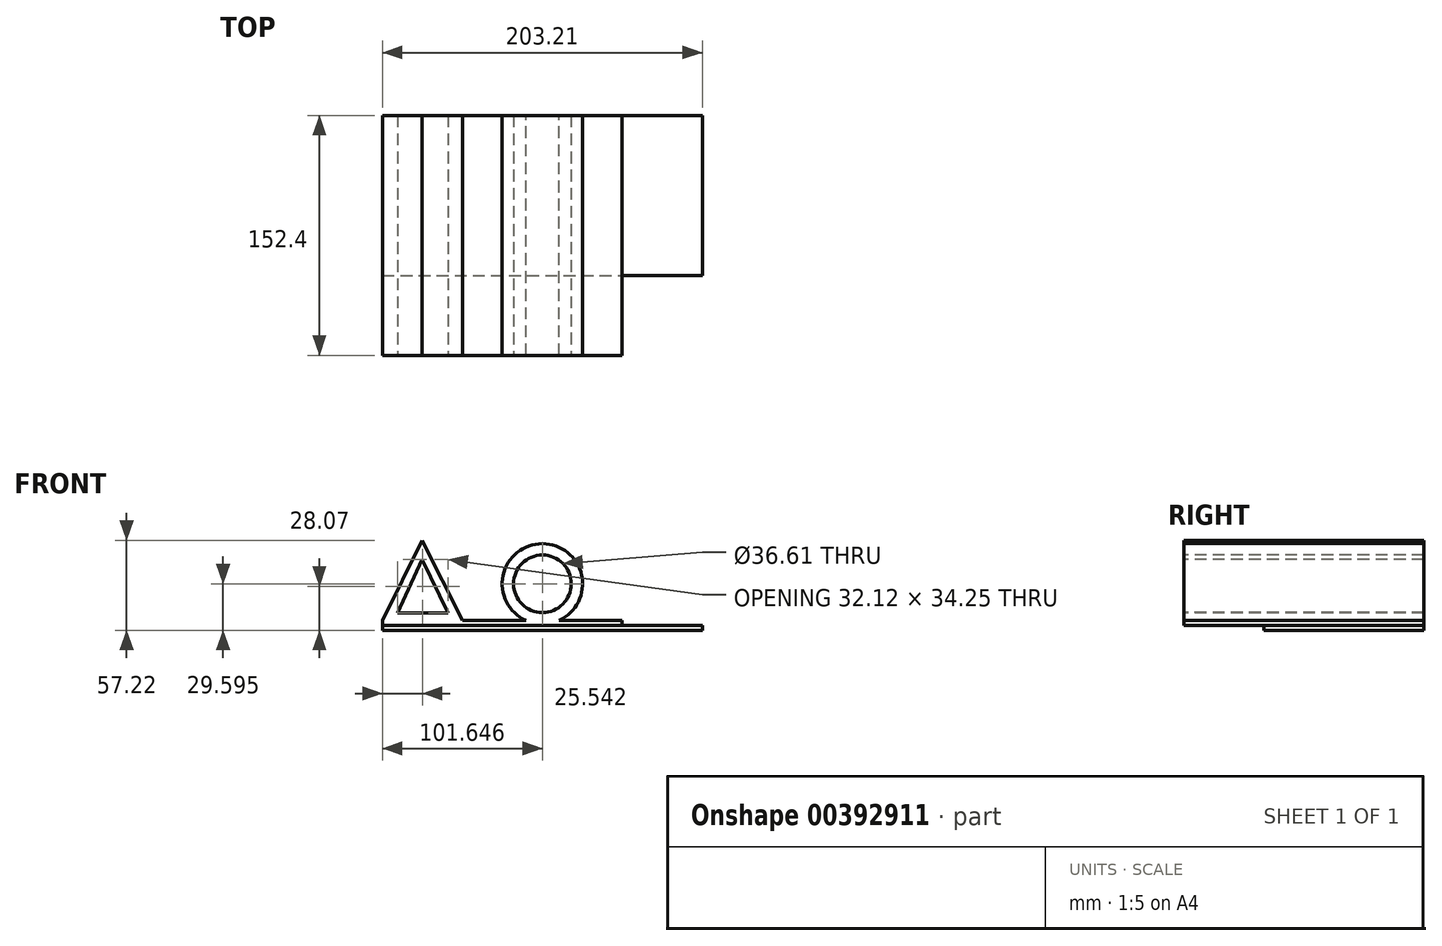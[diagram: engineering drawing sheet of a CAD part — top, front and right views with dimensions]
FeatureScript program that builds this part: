
annotation { "Feature Type Name" : "Feature", "Feature Type Description" : "" }
export const myFeature = defineFeature(function(context is Context, id is Id, definition is map)
    precondition{}
    {
        {
            var Q0;
            Q0=qCreatedBy(makeId("Top.planeOp"),FACE);
            var sketch = newSketch(context, id + "F0", { "sketchPlane" : qUnion([Q0])});
            skLineSegment(sketch, "E0.bottom", {"start": v(101.6, -152.4) * mm, "end": v(-101.6, -152.4) * mm});
            skLineSegment(sketch, "E0.top", {"start": v(101.6, 152.4) * mm, "end": v(-101.6, 152.4) * mm});
            skLineSegment(sketch, "E0.left", {"start": v(101.6, -152.4) * mm, "end": v(101.6, 152.4) * mm});
            skLineSegment(sketch, "E0.right", {"start": v(-101.6, -152.4) * mm, "end": v(-101.6, 152.4) * mm});
            skPoint(sketch, "E0.middle", {"position": v(0, 0) * mm});
            skSolve(sketch);
        }
        {
            var Q0;
            Q0=makeQuery(id+"F0.imprint","IMPRINT",FACE,{"disambiguationData":[TD([[makeQuery(id+"F0.imprint","IMPRINT",EDGE,{"derivedFrom":sQuery(id+"F0.wireOp",EDGE,"E0.bottom")}),-1.0]])]});
            extrude(context, id + "F1", {"entities" : qUnion([Q0]), "depth" : 6.35 * mm});
        }
        {
            var Q0;
            Q0=qCreatedBy(makeId("Front.planeOp"),FACE);
            var sketch = newSketch(context, id + "F2", { "sketchPlane" : qUnion([Q0])});
            skLineSegment(sketch, "E1", {"start": v(-101.61, 6.34) * mm, "end": v(-76.26, 57.22) * mm});
            skLineSegment(sketch, "E2", {"start": v(-76.26, 57.22) * mm, "end": v(-50.83, 6.31) * mm});
            skLineSegment(sketch, "E3", {"start": v(-50.83, 6.31) * mm, "end": v(-101.61, 6.34) * mm});
            skSolve(sketch);
        }
        {
            var Q0;
            Q0=makeQuery(id+"F2.imprint","IMPRINT",FACE,{"disambiguationData":[TD([[makeQuery(id+"F2.imprint","IMPRINT",EDGE,{"derivedFrom":sQuery(id+"F2.wireOp",EDGE,"E1")}),-1.0]])]});
            extrude(context, id + "F3", {"entities" : qUnion([Q0]), "operationType" : NewBodyOperationType.ADD, "depth" : 101.6 * mm});
        }
        {
            var Q0;
            Q0=makeQuery(id+"F3.opExtrude","CAP_FACE",FACE,{"disambiguationData":[OSD([sQuery(id+"F2.wireOp",EDGE,"E1"),sQuery(id+"F2.wireOp",EDGE,"E2"),sQuery(id+"F2.wireOp",EDGE,"E3")])],"isStart":true});
            extrude(context, id + "F4", {"entities" : qUnion([Q0]), "operationType" : NewBodyOperationType.ADD, "depth" : 50.8 * mm});
        }
        {
            var Q0;
            Q0=qCreatedBy(makeId("Front.planeOp"),FACE);
            var sketch = newSketch(context, id + "F5", { "sketchPlane" : qUnion([Q0])});
            skLineSegment(sketch, "E4", {"start": v(-92.13, 10.94) * mm, "end": v(-60, 10.94) * mm});
            skLineSegment(sketch, "E5", {"start": v(-60, 10.94) * mm, "end": v(-76.4, 45.2) * mm});
            skLineSegment(sketch, "E6", {"start": v(-76.4, 45.2) * mm, "end": v(-92.13, 10.94) * mm});
            skSolve(sketch);
        }
        {
            var Q0;
            Q0=qSketchRegion(id+"F5",true);
            extrude(context, id + "F6", {"entities" : qUnion([Q0]), "operationType" : NewBodyOperationType.REMOVE, "endBound" : BoundingType.SYMMETRIC, "oppositeDirection" : true, "depth" : 203.2 * mm});
        }
        {
            var Q0;
            Q0=qCreatedBy(makeId("Front.planeOp"),FACE);
            var sketch = newSketch(context, id + "F7", { "sketchPlane" : qUnion([Q0])});
            skCircle(sketch, "E7", {"center": v(0.04, 29.6) * mm, "radius": 25.53 * mm});
            skSolve(sketch);
        }
        {
            var Q0;
            Q0=makeQuery(id+"F7.imprint","IMPRINT",FACE,{"disambiguationData":[TD([[makeQuery(id+"F7.imprint","IMPRINT",EDGE,{"derivedFrom":sQuery(id+"F7.wireOp",EDGE,"E7")}),1.0]])]});
            extrude(context, id + "F8", {"entities" : qUnion([Q0]), "operationType" : NewBodyOperationType.ADD, "depth" : 101.6 * mm});
        }
        {
            var Q0;
            Q0=makeQuery(id+"F8.opExtrude","CAP_FACE",FACE,{"disambiguationData":[OSD([sQuery(id+"F7.wireOp",EDGE,"E7")])],"isStart":true});
            extrude(context, id + "F9", {"entities" : qUnion([Q0]), "operationType" : NewBodyOperationType.ADD, "depth" : 50.8 * mm});
        }
        {
            var Q0;
            Q0=makeQuery(id+"F8.boolean.opBoolean","MERGE",FACE,{"derivedFrom":[makeQuery(id+"F3.boolean.opBoolean","MERGE",FACE,{"derivedFrom":[makeQuery(id+"F1.opExtrude","SWEPT_FACE",FACE,{"disambiguationData":[OSD([sQuery(id+"F0.wireOp",EDGE,"E0.bottom")])]}),makeQuery(id+"F3.opExtrude","CAP_FACE",FACE,{"disambiguationData":[OSD([sQuery(id+"F2.wireOp",EDGE,"E1"),sQuery(id+"F2.wireOp",EDGE,"E2"),sQuery(id+"F2.wireOp",EDGE,"E3")])],"isStart":false})]}),makeQuery(id+"F8.opExtrude","CAP_FACE",FACE,{"disambiguationData":[OSD([sQuery(id+"F7.wireOp",EDGE,"E7")])],"isStart":false})]});
            var sketch = newSketch(context, id + "F10", { "sketchPlane" : qUnion([Q0])});
            skCircle(sketch, "E8", {"center": v(0.04, 29.6) * mm, "radius": 18.3 * mm});
            skSolve(sketch);
        }
        {
            var Q0;
            Q0=makeQuery(id+"F10.imprint","IMPRINT",FACE,{"disambiguationData":[TD([[makeQuery(id+"F10.imprint","IMPRINT",EDGE,{"derivedFrom":sQuery(id+"F10.wireOp",EDGE,"E8")}),1.0]])]});
            var Q1;
            Q1=sQuery(id+"F10.wireOp",EDGE,"E8");
            extrude(context, id + "F11", {"entities" : qUnion([Q0]), "operationType" : NewBodyOperationType.REMOVE, "surfaceEntities" : qUnion([Q1]), "oppositeDirection" : true, "depth" : 203.2 * mm});
        }
        {
            var Q0;
            Q0=makeQuery(id+"F1.opExtrude","CAP_FACE",FACE,{"disambiguationData":[OSD([sQuery(id+"F0.wireOp",EDGE,"E0.bottom"),sQuery(id+"F0.wireOp",EDGE,"E0.top"),sQuery(id+"F0.wireOp",EDGE,"E0.left"),sQuery(id+"F0.wireOp",EDGE,"E0.right")])],"isStart":false});
            var sketch = newSketch(context, id + "F12", { "sketchPlane" : qUnion([Q0])});
            skLineSegment(sketch, "E9.bottom", {"start": v(-101.6, 152.4) * mm, "end": v(101.6, 152.4) * mm});
            skLineSegment(sketch, "E9.top", {"start": v(-101.6, 50.8) * mm, "end": v(101.6, 50.8) * mm});
            skLineSegment(sketch, "E9.left", {"start": v(-101.6, 152.4) * mm, "end": v(-101.6, 50.8) * mm});
            skLineSegment(sketch, "E9.right", {"start": v(101.6, 152.4) * mm, "end": v(101.6, 50.8) * mm});
            skSolve(sketch);
        }
        {
            var Q0;
            Q0=makeQuery(id+"F1.opExtrude","CAP_FACE",FACE,{"disambiguationData":[OSD([sQuery(id+"F0.wireOp",EDGE,"E0.bottom"),sQuery(id+"F0.wireOp",EDGE,"E0.top"),sQuery(id+"F0.wireOp",EDGE,"E0.left"),sQuery(id+"F0.wireOp",EDGE,"E0.right")])],"isStart":true});
            var sketch = newSketch(context, id + "F13", { "sketchPlane" : qUnion([Q0])});
            skLineSegment(sketch, "E10.bottom", {"start": v(-101.6, 152.4) * mm, "end": v(101.6, 152.4) * mm});
            skLineSegment(sketch, "E10.top", {"start": v(-101.6, 101.6) * mm, "end": v(101.6, 101.6) * mm});
            skLineSegment(sketch, "E10.left", {"start": v(-101.6, 152.4) * mm, "end": v(-101.6, 101.6) * mm});
            skLineSegment(sketch, "E10.right", {"start": v(101.6, 152.4) * mm, "end": v(101.6, 101.6) * mm});
            skSolve(sketch);
        }
        {
            var Q0;
            Q0=makeQuery(id+"F13.imprint","IMPRINT",FACE,{"disambiguationData":[TD([[makeQuery(id+"F13.imprint","IMPRINT",EDGE,{"derivedFrom":sQuery(id+"F13.wireOp",EDGE,"E10.bottom")}),1.0]])]});
            extrude(context, id + "F14", {"entities" : qUnion([Q0]), "operationType" : NewBodyOperationType.REMOVE, "oppositeDirection" : true, "depth" : 81.28 * mm});
        }
        {
            var Q0;
            Q0=makeQuery(id+"F1.opExtrude","CAP_FACE",FACE,{"disambiguationData":[OSD([sQuery(id+"F0.wireOp",EDGE,"E0.bottom"),sQuery(id+"F0.wireOp",EDGE,"E0.top"),sQuery(id+"F0.wireOp",EDGE,"E0.left"),sQuery(id+"F0.wireOp",EDGE,"E0.right")])],"isStart":true});
            var sketch = newSketch(context, id + "F15", { "sketchPlane" : qUnion([Q0])});
            skLineSegment(sketch, "E11.bottom", {"start": v(-101.6, 101.6) * mm, "end": v(101.6, 101.6) * mm});
            skLineSegment(sketch, "E11.top", {"start": v(-101.6, 50.8) * mm, "end": v(101.6, 50.8) * mm});
            skLineSegment(sketch, "E11.left", {"start": v(-101.6, 101.6) * mm, "end": v(-101.6, 50.8) * mm});
            skLineSegment(sketch, "E11.right", {"start": v(101.6, 101.6) * mm, "end": v(101.6, 50.8) * mm});
            skSolve(sketch);
        }
        {
            var Q0;
            Q0=makeQuery(id+"F15.imprint","IMPRINT",FACE,{"disambiguationData":[TD([[makeQuery(id+"F15.imprint","IMPRINT",EDGE,{"derivedFrom":sQuery(id+"F15.wireOp",EDGE,"E11.bottom")}),-1.0]])]});
            extrude(context, id + "F16", {"entities" : qUnion([Q0]), "operationType" : NewBodyOperationType.REMOVE, "oppositeDirection" : true, "depth" : 3.17 * mm});
        }
        {
            var Q0;
            Q0=makeQuery(id+"F1.opExtrude","CAP_FACE",FACE,{"disambiguationData":[OSD([sQuery(id+"F0.wireOp",EDGE,"E0.bottom"),sQuery(id+"F0.wireOp",EDGE,"E0.top"),sQuery(id+"F0.wireOp",EDGE,"E0.left"),sQuery(id+"F0.wireOp",EDGE,"E0.right")])],"isStart":true});
            var sketch = newSketch(context, id + "F17", { "sketchPlane" : qUnion([Q0])});
            skLineSegment(sketch, "E12.bottom", {"start": v(101.6, -152.4) * mm, "end": v(-101.6, -152.4) * mm});
            skLineSegment(sketch, "E12.top", {"start": v(101.6, -50.8) * mm, "end": v(-101.6, -50.8) * mm});
            skLineSegment(sketch, "E12.left", {"start": v(101.6, -152.4) * mm, "end": v(101.6, -50.8) * mm});
            skLineSegment(sketch, "E12.right", {"start": v(-101.6, -152.4) * mm, "end": v(-101.6, -50.8) * mm});
            skSolve(sketch);
        }
        {
            var Q0;
            Q0=makeQuery(id+"F17.imprint","IMPRINT",FACE,{"disambiguationData":[TD([[makeQuery(id+"F17.imprint","IMPRINT",EDGE,{"derivedFrom":sQuery(id+"F17.wireOp",EDGE,"E12.bottom")}),-1.0]])]});
            extrude(context, id + "F18", {"entities" : qUnion([Q0]), "operationType" : NewBodyOperationType.REMOVE, "oppositeDirection" : true, "depth" : 80.26 * mm});
        }
        {
            var Q0;
            {var subQ2=sQuery(id+"F0.wireOp",EDGE,"E0.bottom");var subQ3=makeQuery(id+"F1.opExtrude","CAP_EDGE",EDGE,{"disambiguationData":[OSD([subQ2])],"isStart":false});Q0=makeQuery(id+"F12.imprint","IMPRINT",FACE,{"disambiguationData":[TD([[makeQuery(id+"F12.imprint","IMPRINT",EDGE,{"derivedFrom":subQ3}),-1.0]])]});}
            var sketch = newSketch(context, id + "F19", { "sketchPlane" : qUnion([Q0])});
            skLineSegment(sketch, "E13.bottom", {"start": v(101.6, 50.81) * mm, "end": v(50.65, 50.81) * mm});
            skLineSegment(sketch, "E13.top", {"start": v(101.6, -102.98) * mm, "end": v(50.65, -102.98) * mm});
            skLineSegment(sketch, "E13.left", {"start": v(101.6, 50.81) * mm, "end": v(101.6, -102.98) * mm});
            skLineSegment(sketch, "E13.right", {"start": v(50.65, 50.81) * mm, "end": v(50.65, -102.98) * mm});
            skSolve(sketch);
        }
        {
            var Q0;
            Q0 = qSketchRegion(id + "F19", true);
            extrude(context, id + "F20", {"entities" : qUnion([Q0]), "operationType" : NewBodyOperationType.REMOVE, "oppositeDirection" : true, "depth" : 3.17 * mm});
        }
    });
